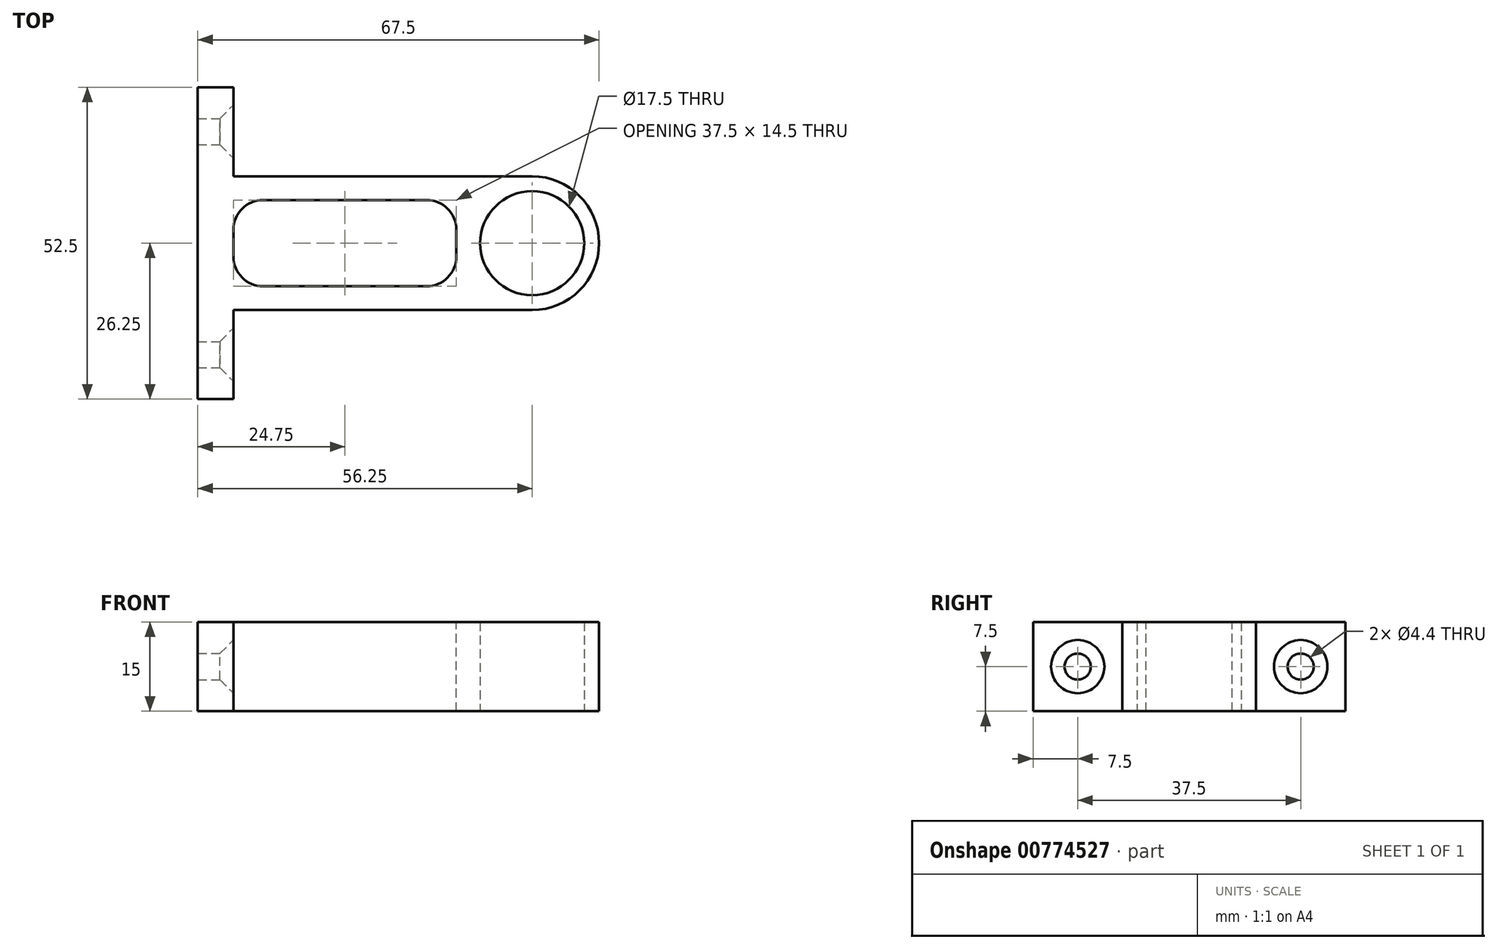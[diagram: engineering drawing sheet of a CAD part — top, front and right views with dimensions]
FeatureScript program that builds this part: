
annotation { "Feature Type Name" : "Feature", "Feature Type Description" : "" }
export const myFeature = defineFeature(function(context is Context, id is Id, definition is map)
    precondition{}
    {
        {
            var Q0;
            Q0=qCreatedBy(makeId("Top.planeOp"),FACE);
            var sketch = newSketch(context, id + "F0", { "sketchPlane" : qUnion([Q0])});
            skCircle(sketch, "E0", {"center": v(0, 0) * mm, "radius": 8.75 * mm});
            skArc(sketch, "E1", {"start": v(0, -11.25) * mm, "mid": v(11.25, 0) * mm, "end": v(0, 11.25) * mm});
            skLineSegment(sketch, "E2", {"start": v(0, 11.25) * mm, "end": v(-50.25, 11.25) * mm});
            skLineSegment(sketch, "E3", {"start": v(0, -11.25) * mm, "end": v(-50.25, -11.25) * mm});
            skLineSegment(sketch, "E4", {"start": v(-50.25, 11.25) * mm, "end": v(-50.25, 26.25) * mm});
            skLineSegment(sketch, "E5", {"start": v(-50.25, 26.25) * mm, "end": v(-56.25, 26.25) * mm});
            skLineSegment(sketch, "E6", {"start": v(-56.25, 26.25) * mm, "end": v(-56.25, -26.25) * mm});
            skLineSegment(sketch, "E7", {"start": v(-56.25, -26.25) * mm, "end": v(-50.25, -26.25) * mm});
            skLineSegment(sketch, "E8", {"start": v(-50.25, -26.25) * mm, "end": v(-50.25, -11.25) * mm});
            skSolve(sketch);
        }
        {
            var Q0;
            Q0=makeQuery(id+"F0.imprint","IMPRINT",FACE,{"disambiguationData":[TD([[makeQuery(id+"F0.imprint","IMPRINT",EDGE,{"derivedFrom":sQuery(id+"F0.wireOp",EDGE,"E0")}),-1.0]])]});
            extrude(context, id + "F1", {"entities" : qUnion([Q0]), "depth" : 15 * mm, "offsetDistance" : 25 * mm});
        }
        {
            var Q0;
            Q0=makeQuery(id+"F1.opExtrude","SWEPT_FACE",FACE,{"disambiguationData":[OSD([sQuery(id+"F0.wireOp",EDGE,"E8")])]});
            var sketch = newSketch(context, id + "F2", { "sketchPlane" : qUnion([Q0])});
            skPoint(sketch, "E9", {"position": v(-18.75, 7.5) * mm});
            skPoint(sketch, "E9.positionSnap0", {"position": v(-26.25, 7.5) * mm});
            skPoint(sketch, "E9.positionSnap1", {"position": v(-18.75, 15) * mm});
            skSolve(sketch);
        }
        {
            var Q0;
            Q0=makeQuery(id+"F1.opExtrude","SWEPT_FACE",FACE,{"disambiguationData":[OSD([sQuery(id+"F0.wireOp",EDGE,"E4")])]});
            var sketch = newSketch(context, id + "F3", { "sketchPlane" : qUnion([Q0])});
            skPoint(sketch, "E10", {"position": v(18.75, 7.5) * mm});
            skPoint(sketch, "E10.positionSnap0", {"position": v(26.25, 7.5) * mm});
            skPoint(sketch, "E10.positionSnap1", {"position": v(18.75, 15) * mm});
            skSolve(sketch);
        }
        {
            var Q0;
            Q0=sQuery(id+"F2.wireOp",VERTEX,"E9");
            var Q1;
            Q1=sQuery(id+"F3.wireOp",VERTEX,"E10");
            var Q2;
            Q2=makeQuery(id+"F1.opExtrude","SWEPT_BODY",BODY,{"disambiguationData":[OSD([sQuery(id+"F0.wireOp",EDGE,"E0"),sQuery(id+"F0.wireOp",EDGE,"E1"),sQuery(id+"F0.wireOp",EDGE,"E2"),sQuery(id+"F0.wireOp",EDGE,"E3"),sQuery(id+"F0.wireOp",EDGE,"E4"),sQuery(id+"F0.wireOp",EDGE,"E5"),sQuery(id+"F0.wireOp",EDGE,"E6"),sQuery(id+"F0.wireOp",EDGE,"E7"),sQuery(id+"F0.wireOp",EDGE,"E8")])]});
            hole(context, id + "F4", {"style" : HoleStyle.C_SINK, "endStyle" : HoleEndStyle.THROUGH, "standardTappedOrClearance" : lookupTablePath({ "standard" : "ISO", "fit" : "Normal", "size" : "M4", "type" : "Clearance" }), "standardBlindInLast" : lookupTablePath({ "fit" : "Standard", "standard" : "ISO", "size" : "M4", "type" : "Clearance" }), "holeDiameter" : 4.4 * mm, "cSinkDiameter" : 8.96 * mm, "cSinkAngle" : 90 * degree, "majorDiameter" : 5 * mm, "isTappedThrough" : true, "tappedDepth" : 12 * mm, "tapClearance" : 3, "locations" : qUnion([Q0, Q1]), "scope" : qUnion([Q2])});
        }
        {
            var Q0;
            Q0=makeQuery(id+"F1.opExtrude","CAP_FACE",FACE,{"disambiguationData":[OSD([sQuery(id+"F0.wireOp",EDGE,"E0"),sQuery(id+"F0.wireOp",EDGE,"E1"),sQuery(id+"F0.wireOp",EDGE,"E2"),sQuery(id+"F0.wireOp",EDGE,"E3"),sQuery(id+"F0.wireOp",EDGE,"E4"),sQuery(id+"F0.wireOp",EDGE,"E5"),sQuery(id+"F0.wireOp",EDGE,"E6"),sQuery(id+"F0.wireOp",EDGE,"E7"),sQuery(id+"F0.wireOp",EDGE,"E8")])],"isStart":false});
            var sketch = newSketch(context, id + "F5", { "sketchPlane" : qUnion([Q0])});
            skLineSegment(sketch, "E11.bottom", {"start": v(-50.25, -7.25) * mm, "end": v(-12.75, -7.25) * mm});
            skLineSegment(sketch, "E11.top", {"start": v(-50.25, 7.25) * mm, "end": v(-12.75, 7.25) * mm});
            skLineSegment(sketch, "E11.left", {"start": v(-50.25, -7.25) * mm, "end": v(-50.25, 7.25) * mm});
            skLineSegment(sketch, "E11.right", {"start": v(-12.75, -7.25) * mm, "end": v(-12.75, 7.25) * mm});
            skLineSegment(sketch, "E12", {"start": v(-50.25, 0) * mm, "end": v(-56.25, 0) * mm, "construction": true});
            skPoint(sketch, "E12.endSnap0", {"position": v(-50.25, 0) * mm});
            skSolve(sketch);
        }
        {
            var Q0;
            Q0=makeQuery(id+"F5.imprint","IMPRINT",FACE,{"disambiguationData":[TD([[makeQuery(id+"F5.imprint","IMPRINT",EDGE,{"derivedFrom":sQuery(id+"F5.wireOp",EDGE,"E11.bottom")}),1.0]])]});
            extrude(context, id + "F6", {"entities" : qUnion([Q0]), "operationType" : NewBodyOperationType.REMOVE, "oppositeDirection" : true, "depth" : 25 * mm, "offsetDistance" : 25 * mm});
        }
        {
            var Q0;
            Q0=makeQuery(id+"F6.boolean.opBoolean","COPY",EDGE,{"derivedFrom":makeQuery(id+"F6.opExtrude","SWEPT_EDGE",EDGE,{"disambiguationData":[OSD([sQuery(id+"F5.wireOp",EDGE,"E11.top"),sQuery(id+"F5.wireOp",EDGE,"E11.left")])]})});
            var Q1;
            Q1=makeQuery(id+"F6.boolean.opBoolean","COPY",EDGE,{"derivedFrom":makeQuery(id+"F6.opExtrude","SWEPT_EDGE",EDGE,{"disambiguationData":[OSD([sQuery(id+"F5.wireOp",EDGE,"E11.bottom"),sQuery(id+"F5.wireOp",EDGE,"E11.left")])]})});
            var Q2;
            Q2=makeQuery(id+"F6.boolean.opBoolean","COPY",EDGE,{"derivedFrom":makeQuery(id+"F6.opExtrude","SWEPT_EDGE",EDGE,{"disambiguationData":[OSD([sQuery(id+"F5.wireOp",EDGE,"E11.top"),sQuery(id+"F5.wireOp",EDGE,"E11.right")])]})});
            var Q3;
            Q3=makeQuery(id+"F6.boolean.opBoolean","COPY",EDGE,{"derivedFrom":makeQuery(id+"F6.opExtrude","SWEPT_EDGE",EDGE,{"disambiguationData":[OSD([sQuery(id+"F5.wireOp",EDGE,"E11.bottom"),sQuery(id+"F5.wireOp",EDGE,"E11.right")])]})});
            fillet(context, id + "F7", {"entities" : qUnion([Q0, Q1, Q2, Q3]), "radius" : 5 * mm, "tangentPropagation" : true, "allowEdgeOverflow" : false});
        }
    });
